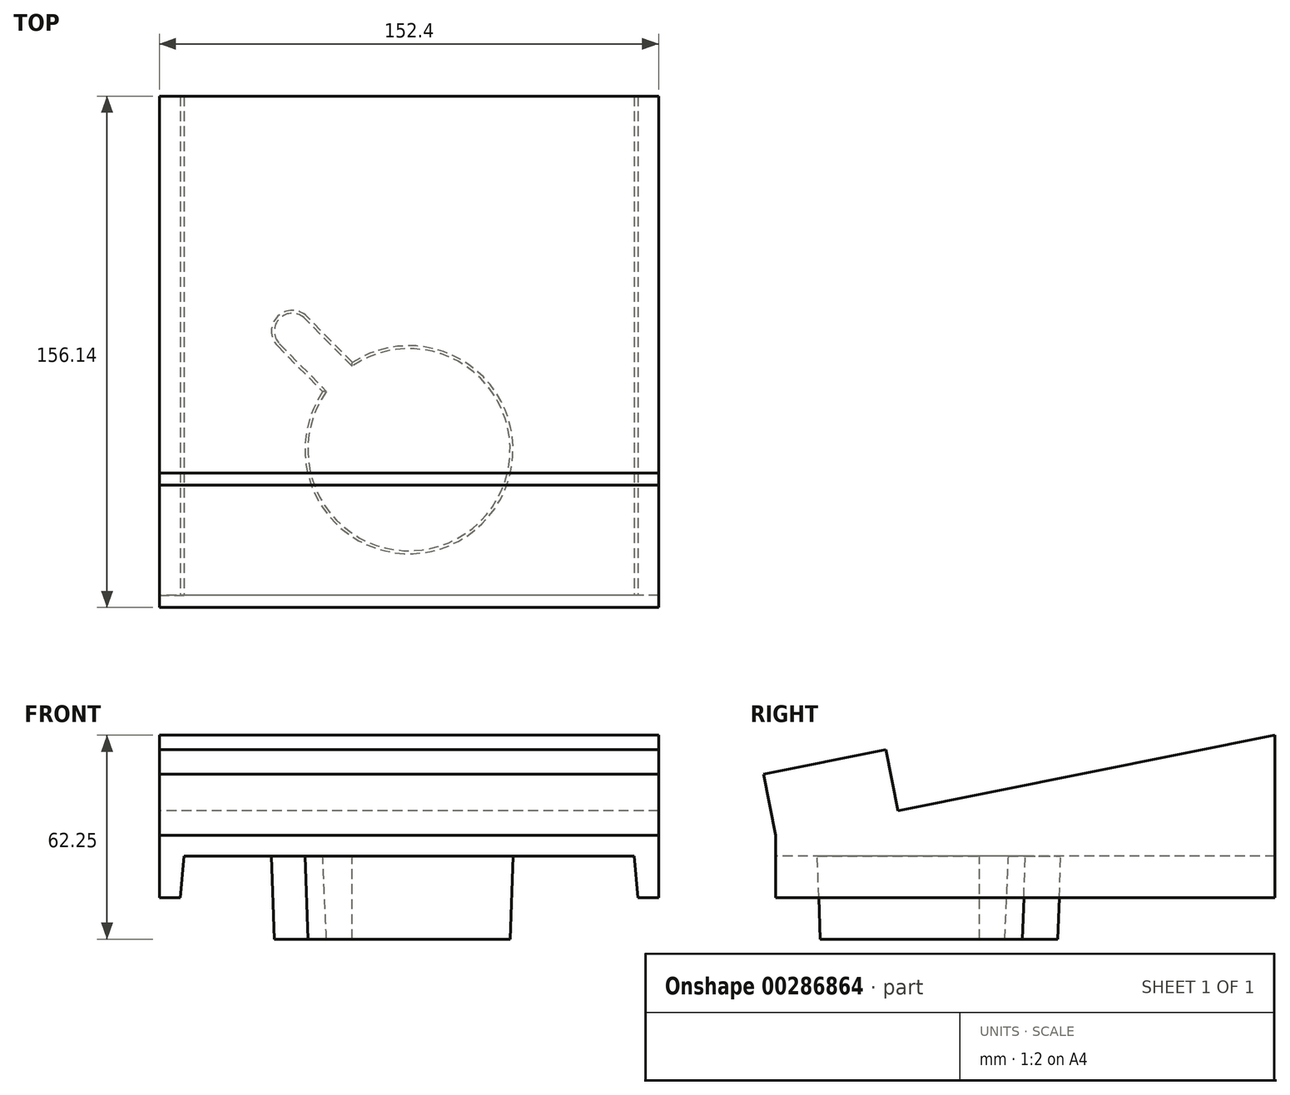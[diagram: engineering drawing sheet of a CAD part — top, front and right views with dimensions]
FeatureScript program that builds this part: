
annotation { "Feature Type Name" : "Feature", "Feature Type Description" : "" }
export const myFeature = defineFeature(function(context is Context, id is Id, definition is map)
    precondition{}
    {
        {
            var Q0;
            Q0=qCreatedBy(makeId("Top.planeOp"),FACE);
            var sketch = newSketch(context, id + "F0", { "sketchPlane" : qUnion([Q0])});
            skLineSegment(sketch, "E0.bottom", {"start": v(76.2, 76.2) * mm, "end": v(-76.2, 76.2) * mm});
            skLineSegment(sketch, "E0.top", {"start": v(76.2, -76.2) * mm, "end": v(-76.2, -76.2) * mm});
            skLineSegment(sketch, "E0.left", {"start": v(76.2, 76.2) * mm, "end": v(76.2, -76.2) * mm});
            skLineSegment(sketch, "E0.right", {"start": v(-76.2, 76.2) * mm, "end": v(-76.2, -76.2) * mm});
            skPoint(sketch, "E0.middle", {"position": v(0, 0) * mm});
            skSolve(sketch);
        }
        {
            var Q0;
            Q0 = qSketchRegion(id + "F0", true);
            extrude(context, id + "F1", {"entities" : qUnion([Q0]), "depth" : 6.35 * mm});
        }
        {
            var Q0;
            Q0=makeQuery(id+"F1.opExtrude","SWEPT_FACE",FACE,{"disambiguationData":[OSD([sQuery(id+"F0.wireOp",EDGE,"E0.right")])]});
            var sketch = newSketch(context, id + "F2", { "sketchPlane" : qUnion([Q0])});
            skLineSegment(sketch, "E1", {"start": v(76.2, 6.35) * mm, "end": v(-76.2, 36.85) * mm});
            skLineSegment(sketch, "E2", {"start": v(-76.2, 6.35) * mm, "end": v(-76.2, 36.85) * mm});
            skLineSegment(sketch, "E3", {"start": v(76.2, 6.35) * mm, "end": v(-76.2, 6.35) * mm});
            skLineSegment(sketch, "E4", {"start": v(38.84, 13.83) * mm, "end": v(42.58, 32.5) * mm});
            skLineSegment(sketch, "E5", {"start": v(42.58, 32.5) * mm, "end": v(79.94, 25.03) * mm});
            skLineSegment(sketch, "E6", {"start": v(79.94, 25.03) * mm, "end": v(76.2, 6.35) * mm});
            skSolve(sketch);
        }
        {
            var Q0;
            Q0 = qSketchRegion(id + "F2", true);
            var Q1;
            Q1=makeQuery(id+"F1.opExtrude","SWEPT_FACE",FACE,{"disambiguationData":[OSD([sQuery(id+"F0.wireOp",EDGE,"E0.left")])]});
            extrude(context, id + "F3", {"entities" : qUnion([Q0]), "operationType" : NewBodyOperationType.ADD, "endBound" : BoundingType.UP_TO_SURFACE, "oppositeDirection" : true, "endBoundEntityFace" : qUnion([Q1]), "depth" : 25.4 * mm});
        }
        {
            var Q0;
            Q0=makeQuery(id+"F1.opExtrude","SWEPT_FACE",FACE,{"disambiguationData":[OSD([sQuery(id+"F0.wireOp",EDGE,"E0.top")])]});
            var sketch = newSketch(context, id + "F4", { "sketchPlane" : qUnion([Q0])});
            skLineSegment(sketch, "E7", {"start": v(0, 0) * mm, "end": v(0, -51.87) * mm, "construction": true});
            skLineSegment(sketch, "E8", {"start": v(-76.2, 0) * mm, "end": v(-76.2, -12.7) * mm});
            skLineSegment(sketch, "E9", {"start": v(-76.2, -12.7) * mm, "end": v(-69.85, -12.7) * mm});
            skLineSegment(sketch, "E10", {"start": v(-69.85, -12.7) * mm, "end": v(-68.74, 0) * mm});
            skLineSegment(sketch, "E11", {"start": v(-68.74, 0) * mm, "end": v(-76.2, 0) * mm});
            skLineSegment(sketch, "E12.MirrorCS", {"start": v(68.74, 0) * mm, "end": v(76.2, 0) * mm});
            skLineSegment(sketch, "E13.MirrorCS", {"start": v(76.2, 0) * mm, "end": v(76.2, -12.7) * mm});
            skLineSegment(sketch, "E14.MirrorCS", {"start": v(76.2, -12.7) * mm, "end": v(69.85, -12.7) * mm});
            skLineSegment(sketch, "E15.MirrorCS", {"start": v(69.85, -12.7) * mm, "end": v(68.74, 0) * mm});
            skSolve(sketch);
        }
        {
            var Q0;
            Q0 = qSketchRegion(id + "F4", true);
            var Q1;
            Q1=makeQuery(id+"F3.boolean.opBoolean","MERGE",FACE,{"derivedFrom":[makeQuery(id+"F1.opExtrude","SWEPT_FACE",FACE,{"disambiguationData":[OSD([sQuery(id+"F0.wireOp",EDGE,"E0.bottom")])]}),makeQuery(id+"F3.opExtrude","SWEPT_FACE",FACE,{"disambiguationData":[OSD([sQuery(id+"F2.wireOp",EDGE,"E2")])]})]});
            extrude(context, id + "F5", {"entities" : qUnion([Q0]), "operationType" : NewBodyOperationType.ADD, "endBound" : BoundingType.UP_TO_SURFACE, "oppositeDirection" : true, "endBoundEntityFace" : qUnion([Q1]), "depth" : 25.4 * mm});
        }
        {
            var Q0;
            Q0=makeQuery(id+"F1.opExtrude","CAP_FACE",FACE,{"disambiguationData":[OSD([sQuery(id+"F0.wireOp",EDGE,"E0.bottom"),sQuery(id+"F0.wireOp",EDGE,"E0.top"),sQuery(id+"F0.wireOp",EDGE,"E0.left"),sQuery(id+"F0.wireOp",EDGE,"E0.right")])],"isStart":true});
            var sketch = newSketch(context, id + "F6", { "sketchPlane" : qUnion([Q0])});
            skCircle(sketch, "E16", {"center": v(0, 31.75) * mm, "radius": 31.75 * mm});
            skLineSegment(sketch, "E17", {"start": v(-26.35, 14.03) * mm, "end": v(-40.16, 0) * mm});
            skLineSegment(sketch, "E18", {"start": v(-40.16, 0) * mm, "end": v(-31.1, -8.9) * mm, "construction": true});
            skLineSegment(sketch, "E19", {"start": v(-31.1, -8.9) * mm, "end": v(-17.3, 5.12) * mm});
            skArc(sketch, "E20", {"start": v(-40.16, 0) * mm, "mid": v(-40.09, -8.98) * mm, "end": v(-31.1, -8.9) * mm});
            skSolve(sketch);
        }
        {
            var Q0;
            Q0 = qSketchRegion(id + "F6", true);
            extrude(context, id + "F7", {"entities" : qUnion([Q0]), "operationType" : NewBodyOperationType.ADD, "depth" : 25.4 * mm, "hasDraft" : true, "draftAngle" : 2 * degree, "draftPullDirection" : true});
        }
    });
